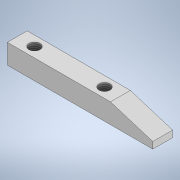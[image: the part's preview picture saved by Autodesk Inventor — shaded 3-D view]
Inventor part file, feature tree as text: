
AUTODESK INVENTOR PART (.ipt)
format: ipt  version: 2021 (Build 250183000, 183)  size: 109,056 bytes
history: native  units: mm
features: sketch x2, other x1, extrude x1, chamfer x1, hole x1
ambient origin geometry x8: Origin, YZ Plane, XZ Plane, XY Plane, X Axis, Y Axis, Z Axis, Center Point
bodies: Body1 (feature_tree)
feature tree (6):
  other  "Sólido1"
  extrude  "Extrusão1"  Depth=15.0mm
  chamfer  "Chanfro1"  Distance=15.0mm
  hole  "Furo1"  [1 undecoded]
  sketch  "Esboço1"  dims[d0=110.0mm d1=15.0mm d2=15.0mm d3=0.0mm]
  sketch  "Esboço2"  dims[d4=10.0mm d5=32.0mm d6=45.0deg d7=7.5mm d8=13.0mm d9=8.376mm d10=20.0mm d11=4.0mm d12=2.0mm d13=90.0deg d14=10.4mm d15=20.594885mm d25=53.0mm]
note: 1 required parameter value undecoded (feature->parameter linkage not recoverable at this tier; creation-order binding heuristic only, values carry confidence <= 0.55)
